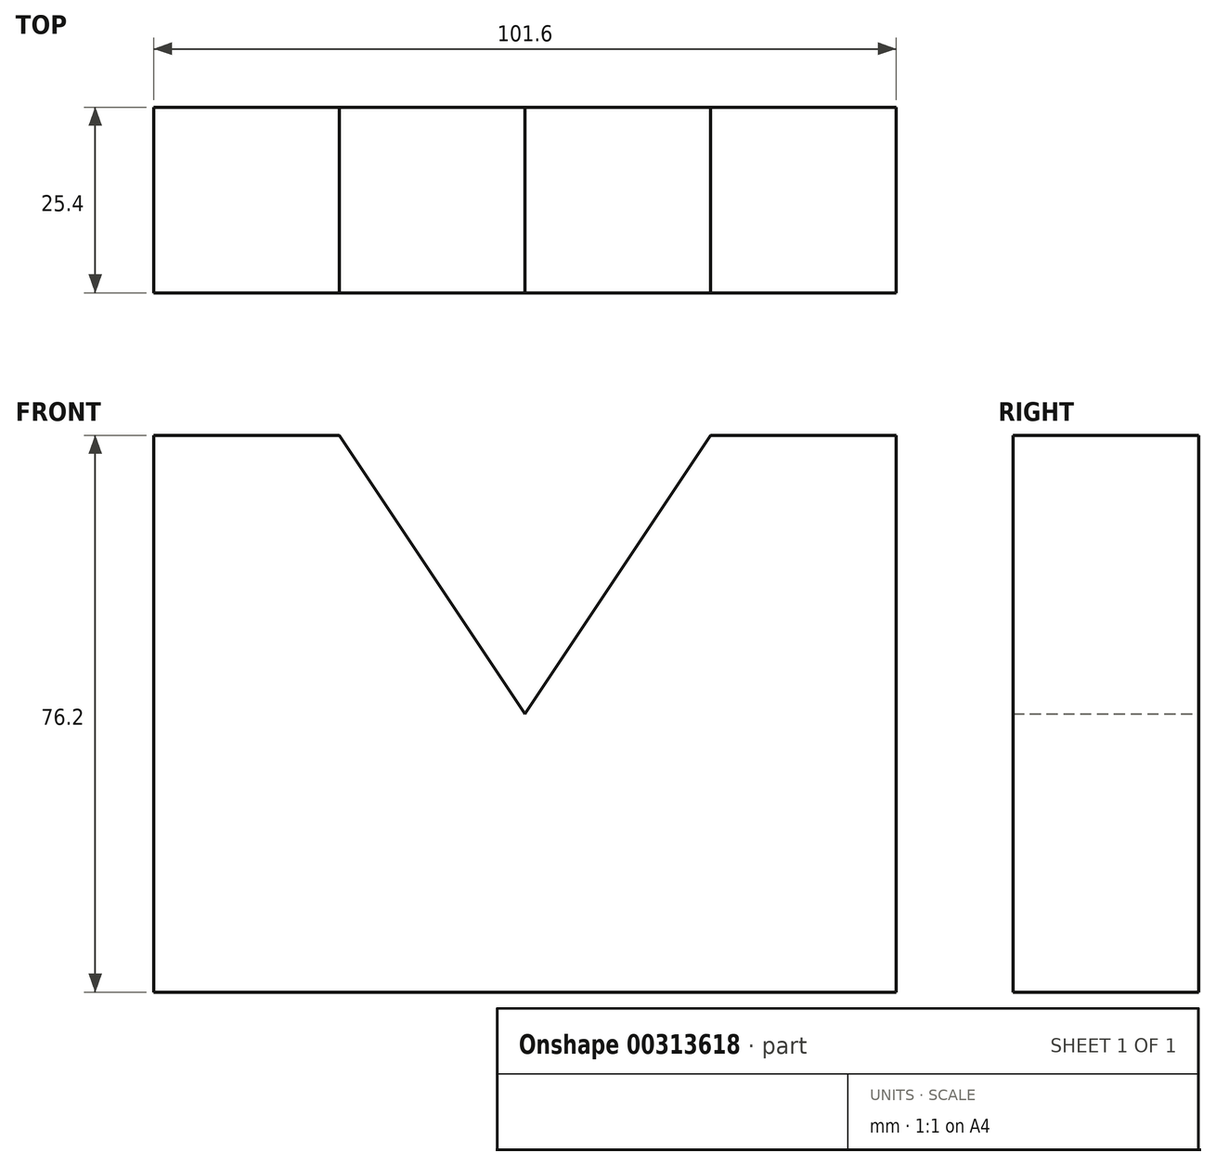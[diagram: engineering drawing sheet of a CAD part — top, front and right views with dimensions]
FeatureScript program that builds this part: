
annotation { "Feature Type Name" : "Feature", "Feature Type Description" : "" }
export const myFeature = defineFeature(function(context is Context, id is Id, definition is map)
    precondition{}
    {
        {
            var Q0;
            Q0=qCreatedBy(makeId("Front.planeOp"),FACE);
            var sketch = newSketch(context, id + "F0", { "sketchPlane" : qUnion([Q0])});
            skLineSegment(sketch, "E0", {"start": v(-41.51, -47.82) * mm, "end": v(60.09, -47.82) * mm});
            skLineSegment(sketch, "E1", {"start": v(60.09, -47.82) * mm, "end": v(60.09, 28.38) * mm});
            skLineSegment(sketch, "E2", {"start": v(60.09, 28.38) * mm, "end": v(34.69, 28.38) * mm});
            skLineSegment(sketch, "E3", {"start": v(-41.51, -47.82) * mm, "end": v(-41.51, 28.38) * mm});
            skLineSegment(sketch, "E4", {"start": v(-41.51, 28.38) * mm, "end": v(-16.11, 28.38) * mm});
            skLineSegment(sketch, "E5", {"start": v(-16.11, 28.38) * mm, "end": v(9.29, -9.72) * mm});
            skPoint(sketch, "E5.endSnap0", {"position": v(60.09, -9.72) * mm});
            skPoint(sketch, "E5.endSnap1", {"position": v(9.29, -47.82) * mm});
            skLineSegment(sketch, "E6", {"start": v(9.29, -9.72) * mm, "end": v(34.69, 28.38) * mm});
            skSolve(sketch);
        }
        {
            var Q0;
            Q0 = qSketchRegion(id + "F0", true);
            extrude(context, id + "F1", {"entities" : qUnion([Q0]), "depth" : 25.4 * mm});
        }
    });
